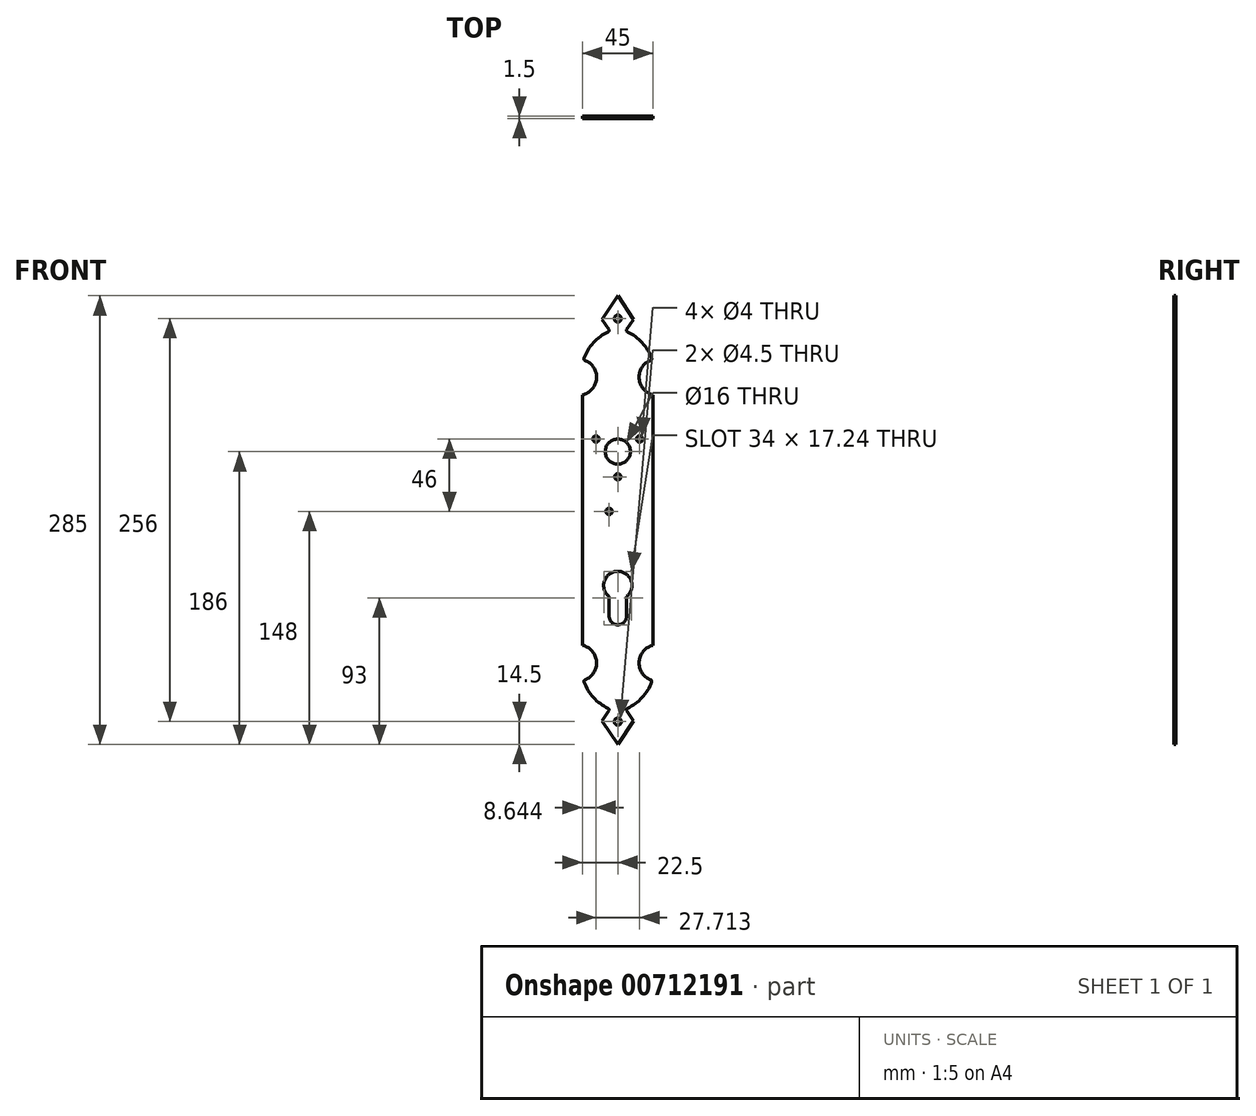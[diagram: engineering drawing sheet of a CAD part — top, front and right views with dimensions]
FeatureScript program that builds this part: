
annotation { "Feature Type Name" : "Feature", "Feature Type Description" : "" }
export const myFeature = defineFeature(function(context is Context, id is Id, definition is map)
    precondition{}
    {
        {
            var Q0;
            Q0=qCreatedBy(makeId("Front.planeOp"),FACE);
            var sketch = newSketch(context, id + "F0", { "sketchPlane" : qUnion([Q0])});
            skLineSegment(sketch, "E0.left", {"start": v(22.5, -79.5) * mm, "end": v(22.5, 79.5) * mm});
            skLineSegment(sketch, "E0.right", {"start": v(-22.5, -79.5) * mm, "end": v(-22.5, 79.5) * mm});
            skPoint(sketch, "E0.middle", {"position": v(0, 0) * mm});
            skLineSegment(sketch, "E1", {"start": v(0, 142.5) * mm, "end": v(-10, 127.5) * mm});
            skLineSegment(sketch, "E2", {"start": v(-10, 127.5) * mm, "end": v(-5.67, 121.06) * mm});
            skArc(sketch, "E3", {"start": v(-6.08, 119.6) * mm, "mid": v(-15.45, 112.71) * mm, "end": v(-21.5, 102.78) * mm});
            skArc(sketch, "E4", {"start": v(-22.5, 79.5) * mm, "mid": v(-13.53, 89.91) * mm, "end": v(-20.92, 101.5) * mm});
            skPoint(sketch, "E5.visualSharp", {"position": v(-5, 120.07) * mm});
            skArc(sketch, "E5.filletArc", {"start": v(-6.08, 119.6) * mm, "mid": v(-5.54, 120.23) * mm, "end": v(-5.67, 121.06) * mm});
            skPoint(sketch, "E6.visualSharp", {"position": v(-21.84, 101.8) * mm});
            skArc(sketch, "E6.filletArc", {"start": v(-21.5, 102.78) * mm, "mid": v(-21.47, 102.02) * mm, "end": v(-20.92, 101.5) * mm});
            skPoint(sketch, "E7.orphan", {"position": v(-22.5, 142.46) * mm});
            skArc(sketch, "E8.MirrorCS", {"start": v(22.5, 79.5) * mm, "mid": v(13.53, 89.91) * mm, "end": v(20.92, 101.5) * mm});
            skArc(sketch, "E9.MirrorCS", {"start": v(21.5, 102.78) * mm, "mid": v(21.47, 102.02) * mm, "end": v(20.92, 101.5) * mm});
            skArc(sketch, "E10.MirrorCS", {"start": v(6.08, 119.6) * mm, "mid": v(15.45, 112.71) * mm, "end": v(21.5, 102.78) * mm});
            skArc(sketch, "E11.MirrorCS", {"start": v(6.08, 119.6) * mm, "mid": v(5.54, 120.23) * mm, "end": v(5.67, 121.06) * mm});
            skLineSegment(sketch, "E12.MirrorCS", {"start": v(0, 142.5) * mm, "end": v(10, 127.5) * mm});
            skLineSegment(sketch, "E13.MirrorCS", {"start": v(10, 127.5) * mm, "end": v(5.67, 121.06) * mm});
            skPoint(sketch, "E14.orphan", {"position": v(22.5, 142.54) * mm});
            skPoint(sketch, "E15.orphan", {"position": v(-23.32, 79.35) * mm});
            skPoint(sketch, "E16.orphan", {"position": v(23.32, 79.35) * mm});
            skPoint(sketch, "E17.orphan", {"position": v(22.5, 93.63) * mm});
            skPoint(sketch, "E18.orphan", {"position": v(-22.5, 93.63) * mm});
            skArc(sketch, "E19.MirrorCS", {"start": v(21.5, -102.78) * mm, "mid": v(21.47, -102.02) * mm, "end": v(20.92, -101.5) * mm});
            skArc(sketch, "E20.MirrorCS", {"start": v(22.5, -79.5) * mm, "mid": v(13.53, -89.91) * mm, "end": v(20.92, -101.5) * mm});
            skArc(sketch, "E21.MirrorCS", {"start": v(6.08, -119.6) * mm, "mid": v(15.45, -112.71) * mm, "end": v(21.5, -102.78) * mm});
            skArc(sketch, "E22.MirrorCS", {"start": v(6.08, -119.6) * mm, "mid": v(5.54, -120.23) * mm, "end": v(5.67, -121.06) * mm});
            skLineSegment(sketch, "E23.MirrorCS", {"start": v(10, -127.5) * mm, "end": v(5.67, -121.06) * mm});
            skLineSegment(sketch, "E24.MirrorCS", {"start": v(0, -142.5) * mm, "end": v(10, -127.5) * mm});
            skLineSegment(sketch, "E25.MirrorCS", {"start": v(-10, -127.5) * mm, "end": v(-5.67, -121.06) * mm});
            skLineSegment(sketch, "E26.MirrorCS", {"start": v(0, -142.5) * mm, "end": v(-10, -127.5) * mm});
            skArc(sketch, "E27.MirrorCS", {"start": v(-6.08, -119.6) * mm, "mid": v(-5.54, -120.23) * mm, "end": v(-5.67, -121.06) * mm});
            skArc(sketch, "E28.MirrorCS", {"start": v(-6.08, -119.6) * mm, "mid": v(-15.45, -112.71) * mm, "end": v(-21.5, -102.78) * mm});
            skArc(sketch, "E29.MirrorCS", {"start": v(-21.5, -102.78) * mm, "mid": v(-21.47, -102.02) * mm, "end": v(-20.92, -101.5) * mm});
            skArc(sketch, "E30.MirrorCS", {"start": v(-22.5, -79.5) * mm, "mid": v(-13.53, -89.91) * mm, "end": v(-20.92, -101.5) * mm});
            skPoint(sketch, "E31.orphan", {"position": v(22.5, -142.46) * mm});
            skPoint(sketch, "E32.orphan", {"position": v(-22.5, -142.54) * mm});
            skPoint(sketch, "E33.orphan", {"position": v(0, 142.5) * mm});
            skCircle(sketch, "E34", {"center": v(0, 128) * mm, "radius": 2.25 * mm});
            skCircle(sketch, "E35.MirrorC", {"center": v(0, -128) * mm, "radius": 2.25 * mm});
            skCircle(sketch, "E36", {"center": v(0, 43.5) * mm, "radius": 8 * mm});
            skCircle(sketch, "E37", {"center": v(0, 43.5) * mm, "radius": 16 * mm, "construction": true});
            skCircle(sketch, "E38", {"center": v(0, 27.5) * mm, "radius": 2 * mm});
            skCircle(sketch, "E39", {"center": v(13.86, 51.5) * mm, "radius": 2 * mm});
            skCircle(sketch, "E40", {"center": v(-13.86, 51.5) * mm, "radius": 2 * mm});
            skLineSegment(sketch, "E41", {"start": v(0, 43.5) * mm, "end": v(-13.86, 51.5) * mm, "construction": true});
            skLineSegment(sketch, "E42", {"start": v(0, 43.5) * mm, "end": v(0, 27.5) * mm, "construction": true});
            skLineSegment(sketch, "E43", {"start": v(0, 43.5) * mm, "end": v(13.86, 51.5) * mm, "construction": true});
            skSolve(sketch);
        }
        {
            var Q0;
            Q0=qSketchRegion(id+"F0",true);
            extrude(context, id + "F1", {"entities" : qUnion([Q0]), "depth" : 1.5 * mm, "offsetDistance" : 25 * mm});
        }
        {
            var Q0;
            Q0=makeQuery(id+"F1.opExtrude","CAP_FACE",FACE,{"disambiguationData":[OSD([sQuery(id+"F0.wireOp",EDGE,"E0.left"),sQuery(id+"F0.wireOp",EDGE,"E0.right"),sQuery(id+"F0.wireOp",EDGE,"E1"),sQuery(id+"F0.wireOp",EDGE,"E2"),sQuery(id+"F0.wireOp",EDGE,"E3"),sQuery(id+"F0.wireOp",EDGE,"E4"),sQuery(id+"F0.wireOp",EDGE,"E5.filletArc"),sQuery(id+"F0.wireOp",EDGE,"E6.filletArc"),sQuery(id+"F0.wireOp",EDGE,"E8.MirrorCS"),sQuery(id+"F0.wireOp",EDGE,"E9.MirrorCS"),sQuery(id+"F0.wireOp",EDGE,"E10.MirrorCS"),sQuery(id+"F0.wireOp",EDGE,"E11.MirrorCS"),sQuery(id+"F0.wireOp",EDGE,"E12.MirrorCS"),sQuery(id+"F0.wireOp",EDGE,"E13.MirrorCS"),sQuery(id+"F0.wireOp",EDGE,"E19.MirrorCS"),sQuery(id+"F0.wireOp",EDGE,"E20.MirrorCS"),sQuery(id+"F0.wireOp",EDGE,"E21.MirrorCS"),sQuery(id+"F0.wireOp",EDGE,"E22.MirrorCS"),sQuery(id+"F0.wireOp",EDGE,"E23.MirrorCS"),sQuery(id+"F0.wireOp",EDGE,"E24.MirrorCS"),sQuery(id+"F0.wireOp",EDGE,"E25.MirrorCS"),sQuery(id+"F0.wireOp",EDGE,"E26.MirrorCS"),sQuery(id+"F0.wireOp",EDGE,"E27.MirrorCS"),sQuery(id+"F0.wireOp",EDGE,"E28.MirrorCS"),sQuery(id+"F0.wireOp",EDGE,"E29.MirrorCS"),sQuery(id+"F0.wireOp",EDGE,"E30.MirrorCS"),sQuery(id+"F0.wireOp",EDGE,"E34"),sQuery(id+"F0.wireOp",EDGE,"E35.MirrorC")])],"isStart":false});
            var sketch = newSketch(context, id + "F2", { "sketchPlane" : qUnion([Q0])});
            skArc(sketch, "E44", {"start": v(5.5, -48.62) * mm, "mid": v(0, -32.5) * mm, "end": v(-5.5, -48.62) * mm});
            skArc(sketch, "E45", {"start": v(-5.5, -61) * mm, "mid": v(0, -66.5) * mm, "end": v(5.5, -61) * mm});
            skLineSegment(sketch, "E46", {"start": v(5.5, -61) * mm, "end": v(5.5, -48.62) * mm});
            skLineSegment(sketch, "E47", {"start": v(-5.5, -61) * mm, "end": v(-5.5, -48.62) * mm});
            skCircle(sketch, "E48", {"center": v(-5.5, 5.5) * mm, "radius": 2 * mm});
            skSolve(sketch);
        }
        {
            var Q0;
            Q0=qSketchRegion(id+"F2",true);
            extrude(context, id + "F3", {"entities" : qUnion([Q0]), "operationType" : NewBodyOperationType.REMOVE, "endBound" : BoundingType.UP_TO_NEXT, "oppositeDirection" : true, "depth" : 25 * mm, "offsetDistance" : 25 * mm});
        }
    });
